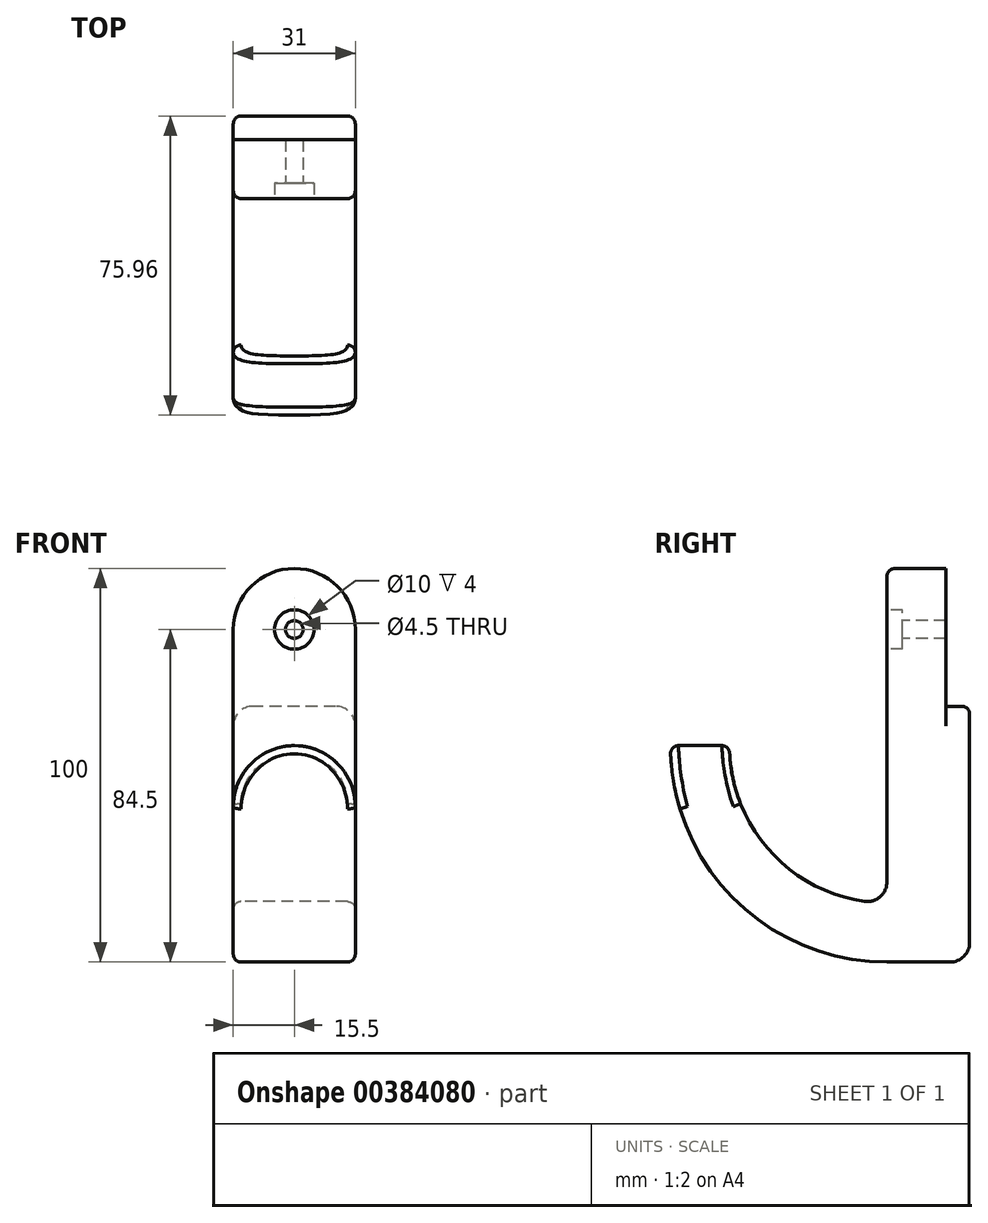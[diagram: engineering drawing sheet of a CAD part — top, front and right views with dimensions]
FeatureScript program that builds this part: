
annotation { "Feature Type Name" : "Feature", "Feature Type Description" : "" }
export const myFeature = defineFeature(function(context is Context, id is Id, definition is map)
    precondition{}
    {
        {
            var Q0;
            Q0=qCreatedBy(makeId("Right.planeOp"),FACE);
            var sketch = newSketch(context, id + "F0", { "sketchPlane" : qUnion([Q0])});
            skLineSegment(sketch, "E0", {"start": v(0, -45) * mm, "end": v(0, 0) * mm});
            skLineSegment(sketch, "E1", {"start": v(0, 0) * mm, "end": v(15, 0) * mm});
            skLineSegment(sketch, "E2", {"start": v(15, 0) * mm, "end": v(15, -100) * mm});
            skArc(sketch, "E3", {"start": v(-40, -45) * mm, "mid": v(-28.28, -73.28) * mm, "end": v(0, -85) * mm});
            skArc(sketch, "E4.0", {"start": v(-55, -45) * mm, "mid": v(-38.9, -83.9) * mm, "end": v(0, -100) * mm});
            skLineSegment(sketch, "E5", {"start": v(0, -45) * mm, "end": v(0, -85) * mm});
            skLineSegment(sketch, "E6", {"start": v(15, -100) * mm, "end": v(0, -100) * mm});
            skLineSegment(sketch, "E7", {"start": v(-55, -45) * mm, "end": v(-40, -45) * mm});
            skLineSegment(sketch, "E8", {"start": v(-55, -45) * mm, "end": v(-55, 27.48) * mm, "construction": true});
            skSolve(sketch);
        }
        {
            var Q0;
            Q0 = qSketchRegion(id + "F0", true);
            extrude(context, id + "F1", {"entities" : qUnion([Q0]), "depth" : 31 * mm});
        }
        {
            var Q0;
            Q0=makeQuery(id+"F1.opExtrude","SWEPT_FACE",FACE,{"disambiguationData":[OSD([sQuery(id+"F0.wireOp",EDGE,"E0"),sQuery(id+"F0.wireOp",EDGE,"E5")])]});
            var sketch = newSketch(context, id + "F2", { "sketchPlane" : qUnion([Q0])});
            skCircle(sketch, "E9", {"center": v(15.5, -15.5) * mm, "radius": 5 * mm});
            skLineSegment(sketch, "E10", {"start": v(15.5, -15.5) * mm, "end": v(15.5, 0) * mm, "construction": true});
            skSolve(sketch);
        }
        {
            var Q0;
            Q0 = qSketchRegion(id + "F2", true);
            extrude(context, id + "F3", {"entities" : qUnion([Q0]), "operationType" : NewBodyOperationType.REMOVE, "oppositeDirection" : true, "depth" : 4 * mm});
        }
        {
            var Q0;
            Q0=makeQuery(id+"F3.boolean.opBoolean","COPY",FACE,{"derivedFrom":makeQuery(id+"F3.opExtrude","CAP_FACE",FACE,{"disambiguationData":[OSD([sQuery(id+"F2.wireOp",EDGE,"E9")])],"isStart":false})});
            var sketch = newSketch(context, id + "F4", { "sketchPlane" : qUnion([Q0])});
            skCircle(sketch, "E11", {"center": v(15.5, -15.5) * mm, "radius": 2.25 * mm});
            skSolve(sketch);
        }
        {
            var Q0;
            Q0 = qSketchRegion(id + "F4", true);
            extrude(context, id + "F5", {"entities" : qUnion([Q0]), "operationType" : NewBodyOperationType.REMOVE, "endBound" : BoundingType.THROUGH_ALL, "oppositeDirection" : true, "depth" : 25 * mm});
        }
        {
            var Q0;
            Q0=makeQuery(id+"F1.opExtrude","SWEPT_FACE",FACE,{"disambiguationData":[OSD([sQuery(id+"F0.wireOp",EDGE,"E2")])]});
            var sketch = newSketch(context, id + "F6", { "sketchPlane" : qUnion([Q0])});
            skLineSegment(sketch, "E12.bottom", {"start": v(-31, -100) * mm, "end": v(0, -100) * mm});
            skLineSegment(sketch, "E12.top", {"start": v(-31, -35) * mm, "end": v(0, -35) * mm});
            skLineSegment(sketch, "E12.left", {"start": v(-31, -100) * mm, "end": v(-31, -35) * mm});
            skLineSegment(sketch, "E12.right", {"start": v(0, -100) * mm, "end": v(0, -35) * mm});
            skLineSegment(sketch, "E13", {"start": v(-15.5, -15.5) * mm, "end": v(-3.44, -15.5) * mm, "construction": true});
            skSolve(sketch);
        }
        {
            var Q0;
            Q0 = qSketchRegion(id + "F6", true);
            extrude(context, id + "F7", {"entities" : qUnion([Q0]), "operationType" : NewBodyOperationType.ADD, "depth" : 6 * mm});
        }
        {
            var Q0;
            Q0=makeQuery(id+"F1.opExtrude","CAP_EDGE",EDGE,{"disambiguationData":[OSD([sQuery(id+"F0.wireOp",EDGE,"E1")])],"isStart":false});
            var Q1;
            Q1=makeQuery(id+"F1.opExtrude","CAP_EDGE",EDGE,{"disambiguationData":[OSD([sQuery(id+"F0.wireOp",EDGE,"E1")])],"isStart":true});
            fillet(context, id + "F8", {"entities" : qUnion([Q0, Q1]), "radius" : (31 / 2) * mm, "tangentPropagation" : true, "allowEdgeOverflow" : false});
        }
        {
            var Q0;
            Q0=makeQuery(id+"F1.opExtrude","CAP_EDGE",EDGE,{"disambiguationData":[OSD([sQuery(id+"F0.wireOp",EDGE,"E7")])],"isStart":false});
            var Q1;
            Q1=makeQuery(id+"F1.opExtrude","CAP_EDGE",EDGE,{"disambiguationData":[OSD([sQuery(id+"F0.wireOp",EDGE,"E7")])],"isStart":true});
            fillet(context, id + "F9", {"entities" : qUnion([Q0, Q1]), "radius" : (31 / 2) * mm, "tangentPropagation" : true, "allowEdgeOverflow" : false});
        }
        {
            var Q0;
            Q0=makeQuery(id+"F1.opExtrude","SWEPT_EDGE",EDGE,{"disambiguationData":[OSD([sQuery(id+"F0.wireOp",EDGE,"E3"),sQuery(id+"F0.wireOp",EDGE,"E5")])]});
            fillet(context, id + "F10", {"entities" : qUnion([Q0]), "radius" : 5 * mm, "tangentPropagation" : true, "allowEdgeOverflow" : false});
        }
        {
            var Q0;
            Q0=makeQuery(id+"F7.opExtrude","CAP_EDGE",EDGE,{"disambiguationData":[OSD([sQuery(id+"F6.wireOp",EDGE,"E12.bottom")])],"isStart":false});
            var Q1;
            Q1=makeQuery(id+"F7.opExtrude","SWEPT_EDGE",EDGE,{"disambiguationData":[OSD([sQuery(id+"F0.wireOp",EDGE,"E2"),sQuery(id+"F6.wireOp",EDGE,"E12.top"),sQuery(id+"F6.wireOp",EDGE,"E12.left")])]});
            var Q2;
            Q2=makeQuery(id+"F7.opExtrude","SWEPT_EDGE",EDGE,{"disambiguationData":[OSD([sQuery(id+"F0.wireOp",EDGE,"E2"),sQuery(id+"F6.wireOp",EDGE,"E12.top"),sQuery(id+"F6.wireOp",EDGE,"E12.right")])]});
            fillet(context, id + "F11", {"entities" : qUnion([Q0, Q1, Q2]), "radius" : 5 * mm, "tangentPropagation" : true, "allowEdgeOverflow" : false});
        }
        {
            var Q0;
            Q0=makeQuery(id+"F8.opFillet","BLEND_EDGE",EDGE,{"blendedFrom":[makeQuery(id+"F1.opExtrude","CAP_EDGE",EDGE,{"disambiguationData":[OSD([sQuery(id+"F0.wireOp",EDGE,"E1")])],"isStart":false}),makeQuery(id+"F1.opExtrude","SWEPT_FACE",FACE,{"disambiguationData":[OSD([sQuery(id+"F0.wireOp",EDGE,"E0"),sQuery(id+"F0.wireOp",EDGE,"E5")])]})],"blendedInto":[makeQuery(id+"F1.opExtrude","SWEPT_FACE",FACE,{"disambiguationData":[OSD([sQuery(id+"F0.wireOp",EDGE,"E0"),sQuery(id+"F0.wireOp",EDGE,"E5")])]})]});
            var Q1;
            Q1=makeQuery(id+"F9.opFillet","BLEND_EDGE",EDGE,{"blendedFrom":[makeQuery(id+"F1.opExtrude","CAP_EDGE",EDGE,{"disambiguationData":[OSD([sQuery(id+"F0.wireOp",EDGE,"E7")])],"isStart":false}),makeQuery(id+"F1.opExtrude","SWEPT_FACE",FACE,{"disambiguationData":[OSD([sQuery(id+"F0.wireOp",EDGE,"E4.0")])]})],"blendedInto":[makeQuery(id+"F1.opExtrude","SWEPT_FACE",FACE,{"disambiguationData":[OSD([sQuery(id+"F0.wireOp",EDGE,"E4.0")])]})]});
            var Q2;
            Q2=makeQuery(id+"F9.opFillet","BLEND_EDGE",EDGE,{"blendedFrom":[makeQuery(id+"F1.opExtrude","CAP_EDGE",EDGE,{"disambiguationData":[OSD([sQuery(id+"F0.wireOp",EDGE,"E7")])],"isStart":false}),makeQuery(id+"F1.opExtrude","SWEPT_FACE",FACE,{"disambiguationData":[OSD([sQuery(id+"F0.wireOp",EDGE,"E3")])]})],"blendedInto":[makeQuery(id+"F1.opExtrude","SWEPT_FACE",FACE,{"disambiguationData":[OSD([sQuery(id+"F0.wireOp",EDGE,"E3")])]})]});
            fillet(context, id + "F12", {"entities" : qUnion([Q0, Q1, Q2]), "radius" : 2 * mm, "tangentPropagation" : true, "allowEdgeOverflow" : false});
        }
    });
